# Revit family: 1240_P-HRIS-KP_nofin_HP
name_source: partatom
category: Doors
revit_build: Autodesk Revit 2016 (Build: 20190507_1515(x64)
units: mm (PartAtom-declared; Revit-internal decimal feet)

## family parameters
Always vertical = Yes
Cut with Voids When Loaded = No
Host = Wall
OmniClass Number = 23.30.20.00
OmniClass Title = Windows
Room Calculation Point = No
Shared = No

## types (39) — shared parameters
Closed = No
Default Sill Height = 0"
Open = Yes
Wall Closure = By host

## per-type parameters (varying)
| type | Bar set | HSB | Height | Sash Width | Setback | Width_x |
| 96X96 | 39 1/4" | 12" | 96" | 36 1/4" | 1 1/8" | 96" |
| 35X92Min | 23" | 12" | 92" | 20" | 1 7/8" | 35" |
| 35X96 | 23" | 12" | 96" | 20" | 1 7/8" | 35" |
| 96X92 | 39 1/4" | 12" | 92" | 36 1/4" | 1 7/8" | 96" |
| 42X96 | 30" | 12" | 96" | 27" | 1 7/8" | 42" |
| 48X92 | 36" | 12" | 92" | 33" | 1 7/8" | 48" |
| 48X96 | 36" | 12" | 96" | 33" | 1 7/8" | 48" |
| 90X92 | 39 1/4" | 12" | 92" | 36 1/4" | 1 7/8" | 90" |
| 90X96 | 39 1/4" | 12" | 96" | 36 1/4" | 1 7/8" | 90" |
| 84X92 | 39 1/4" | 12" | 92" | 36 1/4" | 1 7/8" | 84" |
| 84X96 | 39 1/4" | 12" | 96" | 36 1/4" | 1 7/8" | 84" |
| 78X92 | 39 1/4" | 12" | 92" | 36 1/4" | 1 7/8" | 78" |
| 78X96 | 39 1/4" | 12" | 96" | 36 1/4" | 1 7/8" | 78" |
| 66X92 | 39 1/4" | 12" | 92" | 36 1/4" | 1 7/8" | 66" |
| 66X96 | 39 1/4" | 12" | 96" | 36 1/4" | 1 7/8" | 66" |
| 60X92 | 39 1/4" | 12" | 92" | 36 1/4" | 1 7/8" | 60" |
| 60X96 | 39 1/4" | 12" | 96" | 36 1/4" | 1 7/8" | 60" |
| 54X92 | 39 1/4" | 12" | 92" | 36 1/4" | 1 7/8" | 54" |
| 54X96 | 39 1/4" | 12" | 96" | 36 1/4" | 1 7/8" | 54" |
| 72X92 | 39 1/4" | 12" | 92" | 36 1/4" | 1 7/8" | 72" |
| 72X96 | 39 1/4" | 12" | 96" | 36 1/4" | 1 7/8" | 72" |
| 96X120Max | 39 1/4" | 24" | 120" | 36 1/4" | 1 7/8" | 96" |
| 96X102 | 39 1/4" | 18" | 102" | 36 1/4" | 1 7/8" | 96" |
| 96X108 | 39 1/4" | 18" | 108" | 36 1/4" | 1 7/8" | 96" |
| 96X114 | 39 1/4" | 18" | 114" | 36 1/4" | 1 7/8" | 96" |
| 42x92 | 30" | 12" | 92" | 27" | 1 7/8" | 42" |
| 90x102 | 39 1/4" | 12" | 102" | 36 1/4" | 1 7/8" | 90" |
| 90x108 | 39 1/4" | 18" | 108" | 36 1/4" | 1 7/8" | 90" |
| 90x114 | 39 1/4" | 18" | 114" | 36 1/4" | 1 7/8" | 90" |
| 90x120 | 39 1/4" | 24" | 120" | 36 1/4" | 1 7/8" | 90" |
| 84x114 | 39 1/4" | 18" | 114" | 36 1/4" | 1 7/8" | 84" |
| 84x108 | 39 1/4" | 18" | 108" | 36 1/4" | 1 7/8" | 84" |
| 84x102 | 39 1/4" | 12" | 102" | 36 1/4" | 1 7/8" | 84" |
| 78x114 | 39 1/4" | 18" | 114" | 36 1/4" | 1 7/8" | 78" |
| 78x108 | 39 1/4" | 18" | 108" | 36 1/4" | 1 7/8" | 78" |
| 78x102 | 39 1/4" | 12" | 102" | 36 1/4" | 1 7/8" | 78" |
| 72x108 | 39 1/4" | 18" | 108" | 36 1/4" | 1 7/8" | 72" |
| 72x102 | 39 1/4" | 12" | 102" | 36 1/4" | 1 7/8" | 72" |
| 66x102 | 39 1/4" | 12" | 102" | 36 1/4" | 1 7/8" | 66" |

## geometry (parser evidence)
native form markers: Sweep x3
no freeform markers — native parametric forms only
